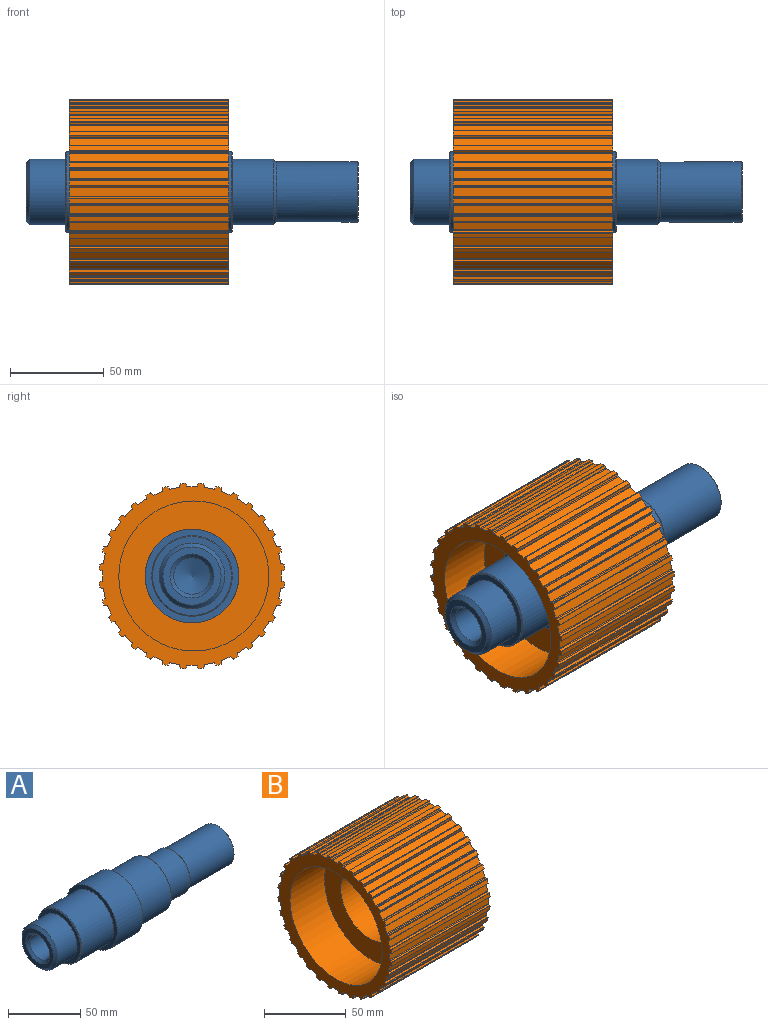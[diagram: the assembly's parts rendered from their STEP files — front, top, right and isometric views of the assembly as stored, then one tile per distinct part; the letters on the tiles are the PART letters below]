
ASSEMBLY  parts=2 mates=1
PART A: 20 faces, bbox 177x50x50 mm
  f0: cylinder r=17.5mm len=35mm, axis (-1,0,0), area 2089.2mm2, adj f14,f15
  f1: plane 31x31mm, normal (-1,0,0), area 321mm2, adj f15,f16
  f2: cylinder r=9.75mm len=92mm, axis (-1,0,0), area 5636mm2, adj f3,f16
  f3: cone r=9.75mm half-angle=70.3deg, axis (-1,0,0), area 317.3mm2, adj f2
  f4: plane 31x31mm, normal (1,0,0), area 754.8mm2, adj f17
  f5: cylinder r=16mm len=43mm, axis (-1,0,0), area 4322.8mm2, adj f6,f17
  f6: torus R=17.5mm, axis (-1,0,0), area 244.9mm2, adj f5,f7
  f7: cylinder r=17.5mm len=35mm, axis (-1,0,0), area 2419mm2, adj f6,f8
  f8: plane 42x42mm, normal (1,0,0), area 423.3mm2, adj f7,f18
  f9: cylinder r=21.5mm len=43mm, axis (-1,0,0), area 4255.3mm2, adj f10,f18
  f10: plane 50x50mm, normal (1,0,0), area 511.3mm2, adj f9,f11
  f11: cylinder r=25mm len=50mm, axis (-1,0,0), area 3927mm2, adj f10,f12
  f12: plane 50x50mm, normal (-1,0,0), area 511.3mm2, adj f11,f13
  f13: cylinder r=21.5mm len=43mm, axis (-1,0,0), area 4255.3mm2, adj f12,f19
  f14: plane 42x42mm, normal (-1,0,0), area 423.3mm2, adj f0,f19
  f15: cone r=15.5mm half-angle=45deg, axis (1,0,0), area 293.2mm2, adj f0,f1
  f16: cone r=9.75mm half-angle=45deg, axis (-1,0,0), area 191mm2, adj f1,f2
  f17: cone r=16mm half-angle=45deg, axis (-1,0,0), area 70mm2, adj f4,f5
  f18: cone r=21.5mm half-angle=45deg, axis (-1,0,0), area 94.4mm2, adj f8,f9
  f19: cone r=21mm half-angle=45deg, axis (1,0,0), area 94.4mm2, adj f13,f14
PART B: 263 faces, bbox 85x98.8x98.8 mm
  f0: cylinder r=0.5mm len=85mm, axis (-1,0,0), area 48.2mm2, adj f219,f220,f224,f257
  f1: cylinder r=0.5mm len=85mm, axis (-1,0,0), area 48.2mm2, adj f215,f216,f224,f257
  f2: cylinder r=0.5mm len=85mm, axis (-1,0,0), area 48.2mm2, adj f211,f212,f224,f257
  f3: cylinder r=0.5mm len=85mm, axis (-1,0,0), area 48.2mm2, adj f207,f208,f224,f257
  f4: cylinder r=0.5mm len=85mm, axis (-1,0,0), area 48.2mm2, adj f53,f203,f224,f257
  f5: cylinder r=0.5mm len=85mm, axis (-1,0,0), area 48.2mm2, adj f199,f202,f224,f257
  f6: cylinder r=0.5mm len=85mm, axis (-1,0,0), area 48.2mm2, adj f195,f198,f224,f257
  f7: cylinder r=0.5mm len=85mm, axis (-1,0,0), area 48.2mm2, adj f191,f194,f224,f257
  f8: cylinder r=0.5mm len=85mm, axis (-1,0,0), area 48.2mm2, adj f163,f164,f224,f257
  f9: cylinder r=0.5mm len=85mm, axis (-1,0,0), area 48.2mm2, adj f159,f160,f224,f257
  f10: cylinder r=0.5mm len=85mm, axis (-1,0,0), area 48.2mm2, adj f155,f156,f224,f257
  f11: cylinder r=0.5mm len=85mm, axis (-1,0,0), area 48.2mm2, adj f151,f152,f224,f257
  f12: cylinder r=0.5mm len=85mm, axis (-1,0,0), area 48.2mm2, adj f147,f148,f224,f257
  f13: cylinder r=0.5mm len=85mm, axis (-1,0,0), area 48.2mm2, adj f137,f140,f224,f257
  f14: cylinder r=0.5mm len=85mm, axis (-1,0,0), area 48.2mm2, adj f133,f136,f224,f257
  f15: cylinder r=0.5mm len=85mm, axis (-1,0,0), area 48.2mm2, adj f129,f132,f224,f257
  f16: cylinder r=0.5mm len=85mm, axis (-1,0,0), area 48.2mm2, adj f125,f128,f224,f257
  f17: cylinder r=0.5mm len=85mm, axis (-1,0,0), area 48.2mm2, adj f121,f124,f224,f257
  f18: cylinder r=0.5mm len=85mm, axis (-1,0,0), area 48.2mm2, adj f94,f223,f224,f257
  f19: cylinder r=1.2mm len=85mm, axis (-1,0,0), area 27.1mm2, adj f208,f224,f256,f257
  f20: cylinder r=1.2mm len=85mm, axis (-1,0,0), area 27.1mm2, adj f202,f224,f229,f257
  f21: cylinder r=1.2mm len=85mm, axis (-1,0,0), area 27.1mm2, adj f198,f224,f230,f257
  f22: cylinder r=1.2mm len=85mm, axis (-1,0,0), area 27.1mm2, adj f194,f224,f231,f257
  f23: cylinder r=1.2mm len=85mm, axis (-1,0,0), area 27.1mm2, adj f164,f224,f236,f257
  f24: cylinder r=1.2mm len=85mm, axis (-1,0,0), area 27.1mm2, adj f160,f224,f237,f257
  f25: cylinder r=1.2mm len=85mm, axis (-1,0,0), area 27.1mm2, adj f156,f224,f238,f257
  f26: cylinder r=1.2mm len=85mm, axis (-1,0,0), area 27.1mm2, adj f152,f224,f239,f257
  f27: cylinder r=1.2mm len=85mm, axis (-1,0,0), area 27.1mm2, adj f148,f224,f240,f257
  f28: cylinder r=1.2mm len=85mm, axis (-1,0,0), area 27.1mm2, adj f145,f224,f242,f257
  f29: cylinder r=1.2mm len=85mm, axis (-1,0,0), area 27.1mm2, adj f144,f224,f241,f257
  f30: cylinder r=1.2mm len=85mm, axis (-1,0,0), area 27.1mm2, adj f140,f224,f243,f257
  f31: cylinder r=1.2mm len=85mm, axis (-1,0,0), area 27.1mm2, adj f136,f224,f244,f257
  f32: cylinder r=1.2mm len=85mm, axis (-1,0,0), area 27.1mm2, adj f132,f224,f245,f257
  f33: cylinder r=1.2mm len=85mm, axis (-1,0,0), area 27.1mm2, adj f128,f224,f246,f257
  f34: cylinder r=1.2mm len=85mm, axis (-1,0,0), area 27.1mm2, adj f124,f224,f247,f257
  f35: cylinder r=1.2mm len=85mm, axis (-1,0,0), area 27.1mm2, adj f94,f224,f252,f257
  f36: cylinder r=1.2mm len=85mm, axis (-1,0,0), area 27.1mm2, adj f220,f224,f253,f257
  f37: cylinder r=1.2mm len=85mm, axis (-1,0,0), area 27.1mm2, adj f216,f224,f254,f257
  f38: cylinder r=1.2mm len=85mm, axis (-1,0,0), area 27.1mm2, adj f212,f224,f255,f257
  f39: cylinder r=1.2mm len=85mm, axis (-1,0,0), area 27.1mm2, adj f53,f224,f228,f257
  f40: cylinder r=0.5mm len=85mm, axis (-1,0,0), area 48.2mm2, adj f52,f205,f224,f257
  f41: cylinder r=1.2mm len=85mm, axis (-1,0,0), area 27.1mm2, adj f205,f224,f227,f257
  f42: cylinder r=1.2mm len=85mm, axis (-1,0,0), area 27.1mm2, adj f44,f224,f226,f257
  f43: cylinder r=1.2mm len=85mm, axis (-1,0,0), area 27.1mm2, adj f45,f224,f225,f257
  f44: plane 85x1.17mm, normal (0,0.91,0.42), area 110mm2, adj f42,f48,f224,f257
  f45: plane 85x1.17mm, normal (0,-0.91,0.42), area 110mm2, adj f43,f46,f224,f257
  f46: cylinder r=0.5mm len=85mm, axis (-1,0,0), area 48.2mm2, adj f45,f47,f224,f257
  f47: plane 85x4.54mm, normal (0,0,1), area 386.2mm2, adj f46,f48,f224,f257
  f48: cylinder r=0.5mm len=85mm, axis (-1,0,0), area 48.2mm2, adj f44,f47,f224,f257
  f49: cylinder r=1.2mm len=85mm, axis (-1,0,0), area 27.1mm2, adj f50,f224,f226,f257
  f50: plane 85x1.26mm, normal (0,-0.97,0.24), area 110mm2, adj f49,f51,f224,f257
  f51: cylinder r=0.5mm len=85mm, axis (-1,0,0), area 48.2mm2, adj f50,f52,f224,f257
  f52: plane 85x4.46mm, normal (0,-0.2,0.98), area 386.2mm2, adj f40,f51,f224,f257
  f53: plane 85x0.95mm, normal (0,0.68,0.74), area 110mm2, adj f4,f39,f224,f257
  f54: plane 85x1.29mm, normal (0,-1,0.04), area 110mm2, adj f55,f204,f224,f257
  f55: cylinder r=1.2mm len=85mm, axis (-1,0,0), area 27.1mm2, adj f54,f224,f227,f257
  f56: cylinder r=1.2mm len=85mm, axis (-1,0,0), area 27.1mm2, adj f213,f224,f256,f257
  f57: cylinder r=1.2mm len=85mm, axis (-1,0,0), area 27.1mm2, adj f217,f224,f255,f257
  f58: cylinder r=1.2mm len=85mm, axis (-1,0,0), area 27.1mm2, adj f221,f224,f254,f257
  f59: cylinder r=1.2mm len=85mm, axis (-1,0,0), area 27.1mm2, adj f95,f224,f253,f257
  f60: cylinder r=1.2mm len=85mm, axis (-1,0,0), area 27.1mm2, adj f99,f224,f251,f257
  f61: cylinder r=1.2mm len=85mm, axis (-1,0,0), area 27.1mm2, adj f100,f224,f252,f257
  f62: cylinder r=1.2mm len=85mm, axis (-1,0,0), area 27.1mm2, adj f104,f224,f250,f257
  f63: cylinder r=1.2mm len=85mm, axis (-1,0,0), area 27.1mm2, adj f105,f224,f251,f257
  f64: cylinder r=1.2mm len=85mm, axis (-1,0,0), area 27.1mm2, adj f109,f224,f249,f257
  f65: cylinder r=1.2mm len=85mm, axis (-1,0,0), area 27.1mm2, adj f110,f224,f250,f257
  f66: cylinder r=1.2mm len=85mm, axis (-1,0,0), area 27.1mm2, adj f114,f224,f248,f257
  f67: cylinder r=1.2mm len=85mm, axis (-1,0,0), area 27.1mm2, adj f115,f224,f249,f257
  f68: cylinder r=1.2mm len=85mm, axis (-1,0,0), area 27.1mm2, adj f119,f224,f247,f257
  f69: cylinder r=1.2mm len=85mm, axis (-1,0,0), area 27.1mm2, adj f120,f224,f248,f257
  f70: cylinder r=1.2mm len=85mm, axis (-1,0,0), area 27.1mm2, adj f123,f224,f246,f257
  f71: cylinder r=1.2mm len=85mm, axis (-1,0,0), area 27.1mm2, adj f127,f224,f245,f257
  f72: cylinder r=1.2mm len=85mm, axis (-1,0,0), area 27.1mm2, adj f131,f224,f244,f257
  f73: cylinder r=1.2mm len=85mm, axis (-1,0,0), area 27.1mm2, adj f135,f224,f243,f257
  f74: cylinder r=1.2mm len=85mm, axis (-1,0,0), area 27.1mm2, adj f139,f224,f242,f257
  f75: cylinder r=1.2mm len=85mm, axis (-1,0,0), area 27.1mm2, adj f149,f224,f241,f257
  f76: cylinder r=1.2mm len=85mm, axis (-1,0,0), area 27.1mm2, adj f153,f224,f240,f257
  f77: cylinder r=1.2mm len=85mm, axis (-1,0,0), area 27.1mm2, adj f157,f224,f239,f257
  f78: cylinder r=1.2mm len=85mm, axis (-1,0,0), area 27.1mm2, adj f161,f224,f238,f257
  f79: cylinder r=1.2mm len=85mm, axis (-1,0,0), area 27.1mm2, adj f165,f224,f237,f257
  f80: cylinder r=1.2mm len=85mm, axis (-1,0,0), area 27.1mm2, adj f169,f224,f235,f257
  f81: cylinder r=1.2mm len=85mm, axis (-1,0,0), area 27.1mm2, adj f170,f224,f236,f257
  f82: cylinder r=1.2mm len=85mm, axis (-1,0,0), area 27.1mm2, adj f174,f224,f234,f257
  f83: cylinder r=1.2mm len=85mm, axis (-1,0,0), area 27.1mm2, adj f175,f224,f235,f257
  f84: cylinder r=1.2mm len=85mm, axis (-1,0,0), area 27.1mm2, adj f179,f224,f233,f257
  f85: cylinder r=1.2mm len=85mm, axis (-1,0,0), area 27.1mm2, adj f180,f224,f234,f257
  f86: cylinder r=1.2mm len=85mm, axis (-1,0,0), area 27.1mm2, adj f184,f224,f232,f257
  f87: cylinder r=1.2mm len=85mm, axis (-1,0,0), area 27.1mm2, adj f185,f224,f233,f257
  f88: cylinder r=1.2mm len=85mm, axis (-1,0,0), area 27.1mm2, adj f189,f224,f231,f257
  f89: cylinder r=1.2mm len=85mm, axis (-1,0,0), area 27.1mm2, adj f190,f224,f232,f257
  f90: cylinder r=1.2mm len=85mm, axis (-1,0,0), area 27.1mm2, adj f193,f224,f230,f257
  f91: cylinder r=1.2mm len=85mm, axis (-1,0,0), area 27.1mm2, adj f197,f224,f229,f257
  f92: cylinder r=1.2mm len=85mm, axis (-1,0,0), area 27.1mm2, adj f201,f224,f228,f257
  f93: cylinder r=1.2mm len=85mm, axis (-1,0,0), area 27.1mm2, adj f209,f224,f225,f257
  f94: plane 85x1.28mm, normal (0,-0.15,0.99), area 110mm2, adj f18,f35,f224,f257
  f95: plane 85x1.11mm, normal (0,0.85,-0.52), area 110mm2, adj f59,f222,f224,f257
  f96: cylinder r=0.5mm len=85mm, axis (-1,0,0), area 48.2mm2, adj f97,f100,f224,f257
  f97: plane 85x4.2mm, normal (0,0.92,0.38), area 386.2mm2, adj f96,f98,f224,f257
  f98: cylinder r=0.5mm len=85mm, axis (-1,0,0), area 48.2mm2, adj f97,f99,f224,f257
  f99: plane 85x1.29mm, normal (0,0.04,1), area 110mm2, adj f60,f98,f224,f257
  f100: plane 85x0.95mm, normal (0,0.74,-0.68), area 110mm2, adj f61,f96,f224,f257
  f101: cylinder r=0.5mm len=85mm, axis (-1,0,0), area 48.2mm2, adj f102,f105,f224,f257
  f102: plane 85x4.46mm, normal (0,0.98,0.2), area 386.2mm2, adj f101,f103,f224,f257
  f103: cylinder r=0.5mm len=85mm, axis (-1,0,0), area 48.2mm2, adj f102,f104,f224,f257
  f104: plane 85x1.26mm, normal (0,0.24,0.97), area 110mm2, adj f62,f103,f224,f257
  f105: plane 85x1.04mm, normal (0,0.59,-0.81), area 110mm2, adj f63,f101,f224,f257
  f106: cylinder r=0.5mm len=85mm, axis (-1,0,0), area 48.2mm2, adj f107,f110,f224,f257
  f107: plane 85x4.54mm, normal (0,1,0), area 386.2mm2, adj f106,f108,f224,f257
  f108: cylinder r=0.5mm len=85mm, axis (-1,0,0), area 48.2mm2, adj f107,f109,f224,f257
  f109: plane 85x1.17mm, normal (0,0.42,0.91), area 110mm2, adj f64,f108,f224,f257
  f110: plane 85x1.17mm, normal (0,0.42,-0.91), area 110mm2, adj f65,f106,f224,f257
  f111: cylinder r=0.5mm len=85mm, axis (-1,0,0), area 48.2mm2, adj f112,f115,f224,f257
  f112: plane 85x4.46mm, normal (0,0.98,-0.2), area 386.2mm2, adj f111,f113,f224,f257
  f113: cylinder r=0.5mm len=85mm, axis (-1,0,0), area 48.2mm2, adj f112,f114,f224,f257
  f114: plane 85x1.04mm, normal (0,0.59,0.81), area 110mm2, adj f66,f113,f224,f257
  f115: plane 85x1.26mm, normal (0,0.24,-0.97), area 110mm2, adj f67,f111,f224,f257
  f116: cylinder r=0.5mm len=85mm, axis (-1,0,0), area 48.2mm2, adj f117,f120,f224,f257
  f117: plane 85x4.2mm, normal (0,0.92,-0.38), area 386.2mm2, adj f116,f118,f224,f257
  f118: cylinder r=0.5mm len=85mm, axis (-1,0,0), area 48.2mm2, adj f117,f119,f224,f257
  f119: plane 85x0.95mm, normal (0,0.74,0.68), area 110mm2, adj f68,f118,f224,f257
  f120: plane 85x1.29mm, normal (0,0.04,-1), area 110mm2, adj f69,f116,f224,f257
  f121: plane 85x3.78mm, normal (0,0.83,-0.56), area 386.2mm2, adj f17,f122,f224,f257
  f122: cylinder r=0.5mm len=85mm, axis (-1,0,0), area 48.2mm2, adj f121,f123,f224,f257
  f123: plane 85x1.11mm, normal (0,0.85,0.52), area 110mm2, adj f70,f122,f224,f257
  f124: plane 85x1.28mm, normal (0,-0.15,-0.99), area 110mm2, adj f17,f34,f224,f257
  f125: plane 85x3.21mm, normal (0,0.71,-0.71), area 386.2mm2, adj f16,f126,f224,f257
  f126: cylinder r=0.5mm len=85mm, axis (-1,0,0), area 48.2mm2, adj f125,f127,f224,f257
  f127: plane 85x1.22mm, normal (0,0.94,0.34), area 110mm2, adj f71,f126,f224,f257
  f128: plane 85x1.22mm, normal (0,-0.34,-0.94), area 110mm2, adj f16,f33,f224,f257
  f129: plane 85x3.78mm, normal (0,0.56,-0.83), area 386.2mm2, adj f15,f130,f224,f257
  f130: cylinder r=0.5mm len=85mm, axis (-1,0,0), area 48.2mm2, adj f129,f131,f224,f257
  f131: plane 85x1.28mm, normal (0,0.99,0.15), area 110mm2, adj f72,f130,f224,f257
  f132: plane 85x1.11mm, normal (0,-0.52,-0.85), area 110mm2, adj f15,f32,f224,f257
  f133: plane 85x4.2mm, normal (0,0.38,-0.92), area 386.2mm2, adj f14,f134,f224,f257
  f134: cylinder r=0.5mm len=85mm, axis (-1,0,0), area 48.2mm2, adj f133,f135,f224,f257
  f135: plane 85x1.29mm, normal (0,1,-0.04), area 110mm2, adj f73,f134,f224,f257
  f136: plane 85x0.95mm, normal (0,-0.68,-0.74), area 110mm2, adj f14,f31,f224,f257
  f137: plane 85x4.46mm, normal (0,0.2,-0.98), area 386.2mm2, adj f13,f138,f224,f257
  f138: cylinder r=0.5mm len=85mm, axis (-1,0,0), area 48.2mm2, adj f137,f139,f224,f257
  f139: plane 85x1.26mm, normal (0,0.97,-0.24), area 110mm2, adj f74,f138,f224,f257
  f140: plane 85x1.04mm, normal (0,-0.81,-0.59), area 110mm2, adj f13,f30,f224,f257
  f141: cylinder r=0.5mm len=85mm, axis (-1,0,0), area 48.2mm2, adj f142,f145,f224,f257
  f142: plane 85x4.54mm, normal (0,0,-1), area 386.2mm2, adj f141,f143,f224,f257
  f143: cylinder r=0.5mm len=85mm, axis (-1,0,0), area 48.2mm2, adj f142,f144,f224,f257
  f144: plane 85x1.17mm, normal (0,0.91,-0.42), area 110mm2, adj f29,f143,f224,f257
  f145: plane 85x1.17mm, normal (0,-0.91,-0.42), area 110mm2, adj f28,f141,f224,f257
  f146: cylinder r=0.5mm len=85mm, axis (-1,0,0), area 48.2mm2, adj f147,f149,f224,f257
  f147: plane 85x4.46mm, normal (0,-0.2,-0.98), area 386.2mm2, adj f12,f146,f224,f257
  f148: plane 85x1.04mm, normal (0,0.81,-0.59), area 110mm2, adj f12,f27,f224,f257
  f149: plane 85x1.26mm, normal (0,-0.97,-0.24), area 110mm2, adj f75,f146,f224,f257
  f150: cylinder r=0.5mm len=85mm, axis (-1,0,0), area 48.2mm2, adj f151,f153,f224,f257
  f151: plane 85x4.2mm, normal (0,-0.38,-0.92), area 386.2mm2, adj f11,f150,f224,f257
  f152: plane 85x0.95mm, normal (0,0.68,-0.74), area 110mm2, adj f11,f26,f224,f257
  f153: plane 85x1.29mm, normal (0,-1,-0.04), area 110mm2, adj f76,f150,f224,f257
  f154: cylinder r=0.5mm len=85mm, axis (-1,0,0), area 48.2mm2, adj f155,f157,f224,f257
  f155: plane 85x3.78mm, normal (0,-0.56,-0.83), area 386.2mm2, adj f10,f154,f224,f257
  f156: plane 85x1.11mm, normal (0,0.52,-0.85), area 110mm2, adj f10,f25,f224,f257
  f157: plane 85x1.28mm, normal (0,-0.99,0.15), area 110mm2, adj f77,f154,f224,f257
  f158: cylinder r=0.5mm len=85mm, axis (-1,0,0), area 48.2mm2, adj f159,f161,f224,f257
  f159: plane 85x3.21mm, normal (0,-0.71,-0.71), area 386.2mm2, adj f9,f158,f224,f257
  f160: plane 85x1.22mm, normal (0,0.34,-0.94), area 110mm2, adj f9,f24,f224,f257
  f161: plane 85x1.22mm, normal (0,-0.94,0.34), area 110mm2, adj f78,f158,f224,f257
  f162: cylinder r=0.5mm len=85mm, axis (-1,0,0), area 48.2mm2, adj f163,f165,f224,f257
  f163: plane 85x3.78mm, normal (0,-0.83,-0.56), area 386.2mm2, adj f8,f162,f224,f257
  f164: plane 85x1.28mm, normal (0,0.15,-0.99), area 110mm2, adj f8,f23,f224,f257
  f165: plane 85x1.11mm, normal (0,-0.85,0.52), area 110mm2, adj f79,f162,f224,f257
  f166: cylinder r=0.5mm len=85mm, axis (-1,0,0), area 48.2mm2, adj f167,f170,f224,f257
  f167: plane 85x4.2mm, normal (0,-0.92,-0.38), area 386.2mm2, adj f166,f168,f224,f257
  f168: cylinder r=0.5mm len=85mm, axis (-1,0,0), area 48.2mm2, adj f167,f169,f224,f257
  f169: plane 85x1.29mm, normal (0,-0.04,-1), area 110mm2, adj f80,f168,f224,f257
  f170: plane 85x0.95mm, normal (0,-0.74,0.68), area 110mm2, adj f81,f166,f224,f257
  f171: cylinder r=0.5mm len=85mm, axis (-1,0,0), area 48.2mm2, adj f172,f175,f224,f257
  f172: plane 85x4.46mm, normal (0,-0.98,-0.2), area 386.2mm2, adj f171,f173,f224,f257
  f173: cylinder r=0.5mm len=85mm, axis (-1,0,0), area 48.2mm2, adj f172,f174,f224,f257
  f174: plane 85x1.26mm, normal (0,-0.24,-0.97), area 110mm2, adj f82,f173,f224,f257
  f175: plane 85x1.04mm, normal (0,-0.59,0.81), area 110mm2, adj f83,f171,f224,f257
  f176: cylinder r=0.5mm len=85mm, axis (-1,0,0), area 48.2mm2, adj f177,f180,f224,f257
  f177: plane 85x4.54mm, normal (0,-1,0), area 386.2mm2, adj f176,f178,f224,f257
  f178: cylinder r=0.5mm len=85mm, axis (-1,0,0), area 48.2mm2, adj f177,f179,f224,f257
  f179: plane 85x1.17mm, normal (0,-0.42,-0.91), area 110mm2, adj f84,f178,f224,f257
  f180: plane 85x1.17mm, normal (0,-0.42,0.91), area 110mm2, adj f85,f176,f224,f257
  f181: cylinder r=0.5mm len=85mm, axis (-1,0,0), area 48.2mm2, adj f182,f185,f224,f257
  f182: plane 85x4.46mm, normal (0,-0.98,0.2), area 386.2mm2, adj f181,f183,f224,f257
  f183: cylinder r=0.5mm len=85mm, axis (-1,0,0), area 48.2mm2, adj f182,f184,f224,f257
  f184: plane 85x1.04mm, normal (0,-0.59,-0.81), area 110mm2, adj f86,f183,f224,f257
  f185: plane 85x1.26mm, normal (0,-0.24,0.97), area 110mm2, adj f87,f181,f224,f257
  f186: cylinder r=0.5mm len=85mm, axis (-1,0,0), area 48.2mm2, adj f187,f190,f224,f257
  f187: plane 85x4.2mm, normal (0,-0.92,0.38), area 386.2mm2, adj f186,f188,f224,f257
  f188: cylinder r=0.5mm len=85mm, axis (-1,0,0), area 48.2mm2, adj f187,f189,f224,f257
  f189: plane 85x0.95mm, normal (0,-0.74,-0.68), area 110mm2, adj f88,f188,f224,f257
  f190: plane 85x1.29mm, normal (0,-0.04,1), area 110mm2, adj f89,f186,f224,f257
  f191: plane 85x3.78mm, normal (0,-0.83,0.56), area 386.2mm2, adj f7,f192,f224,f257
  f192: cylinder r=0.5mm len=85mm, axis (-1,0,0), area 48.2mm2, adj f191,f193,f224,f257
  f193: plane 85x1.11mm, normal (0,-0.85,-0.52), area 110mm2, adj f90,f192,f224,f257
  f194: plane 85x1.28mm, normal (0,0.15,0.99), area 110mm2, adj f7,f22,f224,f257
  f195: plane 85x3.21mm, normal (0,-0.71,0.71), area 386.2mm2, adj f6,f196,f224,f257
  f196: cylinder r=0.5mm len=85mm, axis (-1,0,0), area 48.2mm2, adj f195,f197,f224,f257
  f197: plane 85x1.22mm, normal (0,-0.94,-0.34), area 110mm2, adj f91,f196,f224,f257
  f198: plane 85x1.22mm, normal (0,0.34,0.94), area 110mm2, adj f6,f21,f224,f257
  f199: plane 85x3.78mm, normal (0,-0.56,0.83), area 386.2mm2, adj f5,f200,f224,f257
  f200: cylinder r=0.5mm len=85mm, axis (-1,0,0), area 48.2mm2, adj f199,f201,f224,f257
  f201: plane 85x1.28mm, normal (0,-0.99,-0.15), area 110mm2, adj f92,f200,f224,f257
  f202: plane 85x1.11mm, normal (0,0.52,0.85), area 110mm2, adj f5,f20,f224,f257
  f203: plane 85x4.2mm, normal (0,-0.38,0.92), area 386.2mm2, adj f4,f204,f224,f257
  f204: cylinder r=0.5mm len=85mm, axis (-1,0,0), area 48.2mm2, adj f54,f203,f224,f257
  f205: plane 85x1.04mm, normal (0,0.81,0.59), area 110mm2, adj f40,f41,f224,f257
  f206: cylinder r=0.5mm len=85mm, axis (-1,0,0), area 48.2mm2, adj f207,f209,f224,f257
  f207: plane 85x4.46mm, normal (0,0.2,0.98), area 386.2mm2, adj f3,f206,f224,f257
  f208: plane 85x1.04mm, normal (0,-0.81,0.59), area 110mm2, adj f3,f19,f224,f257
  f209: plane 85x1.26mm, normal (0,0.97,0.24), area 110mm2, adj f93,f206,f224,f257
  f210: cylinder r=0.5mm len=85mm, axis (-1,0,0), area 48.2mm2, adj f211,f213,f224,f257
  f211: plane 85x4.2mm, normal (0,0.38,0.92), area 386.2mm2, adj f2,f210,f224,f257
  f212: plane 85x0.95mm, normal (0,-0.68,0.74), area 110mm2, adj f2,f38,f224,f257
  f213: plane 85x1.29mm, normal (0,1,0.04), area 110mm2, adj f56,f210,f224,f257
  f214: cylinder r=0.5mm len=85mm, axis (-1,0,0), area 48.2mm2, adj f215,f217,f224,f257
  f215: plane 85x3.78mm, normal (0,0.56,0.83), area 386.2mm2, adj f1,f214,f224,f257
  f216: plane 85x1.11mm, normal (0,-0.52,0.85), area 110mm2, adj f1,f37,f224,f257
  f217: plane 85x1.28mm, normal (0,0.99,-0.15), area 110mm2, adj f57,f214,f224,f257
  f218: cylinder r=0.5mm len=85mm, axis (-1,0,0), area 48.2mm2, adj f219,f221,f224,f257
  f219: plane 85x3.21mm, normal (0,0.71,0.71), area 386.2mm2, adj f0,f218,f224,f257
  f220: plane 85x1.22mm, normal (0,-0.34,0.94), area 110mm2, adj f0,f36,f224,f257
  f221: plane 85x1.22mm, normal (0,0.94,-0.34), area 110mm2, adj f58,f218,f224,f257
  f222: cylinder r=0.5mm len=85mm, axis (-1,0,0), area 48.2mm2, adj f95,f223,f224,f257
  f223: plane 85x3.78mm, normal (0,0.83,0.56), area 386.2mm2, adj f18,f222,f224,f257
  f224: plane 98.76x98.76mm, normal (1,0,0), area 2322.9mm2, adj f0,f1,f2,f3,f4,f5,f6,f7
  f225: cylinder r=49.5mm len=85mm, axis (1,0,0), area 240.2mm2, adj f43,f93,f224,f257
  f226: cylinder r=49.5mm len=85mm, axis (1,0,0), area 240.2mm2, adj f42,f49,f224,f257
  f227: cylinder r=49.5mm len=85mm, axis (1,0,0), area 240.2mm2, adj f41,f55,f224,f257
  f228: cylinder r=49.5mm len=85mm, axis (1,0,0), area 240.2mm2, adj f39,f92,f224,f257
  f229: cylinder r=49.5mm len=85mm, axis (1,0,0), area 240.2mm2, adj f20,f91,f224,f257
  f230: cylinder r=49.5mm len=85mm, axis (1,0,0), area 240.2mm2, adj f21,f90,f224,f257
  f231: cylinder r=49.5mm len=85mm, axis (1,0,0), area 240.2mm2, adj f22,f88,f224,f257
  f232: cylinder r=49.5mm len=85mm, axis (1,0,0), area 240.2mm2, adj f86,f89,f224,f257
  f233: cylinder r=49.5mm len=85mm, axis (1,0,0), area 240.2mm2, adj f84,f87,f224,f257
  f234: cylinder r=49.5mm len=85mm, axis (1,0,0), area 240.2mm2, adj f82,f85,f224,f257
  f235: cylinder r=49.5mm len=85mm, axis (1,0,0), area 240.2mm2, adj f80,f83,f224,f257
  f236: cylinder r=49.5mm len=85mm, axis (1,0,0), area 240.2mm2, adj f23,f81,f224,f257
  f237: cylinder r=49.5mm len=85mm, axis (1,0,0), area 240.2mm2, adj f24,f79,f224,f257
  f238: cylinder r=49.5mm len=85mm, axis (1,0,0), area 240.2mm2, adj f25,f78,f224,f257
  f239: cylinder r=49.5mm len=85mm, axis (1,0,0), area 240.2mm2, adj f26,f77,f224,f257
  f240: cylinder r=49.5mm len=85mm, axis (1,0,0), area 240.2mm2, adj f27,f76,f224,f257
  f241: cylinder r=49.5mm len=85mm, axis (1,0,0), area 240.2mm2, adj f29,f75,f224,f257
  f242: cylinder r=49.5mm len=85mm, axis (1,0,0), area 240.2mm2, adj f28,f74,f224,f257
  f243: cylinder r=49.5mm len=85mm, axis (1,0,0), area 240.2mm2, adj f30,f73,f224,f257
  f244: cylinder r=49.5mm len=85mm, axis (1,0,0), area 240.2mm2, adj f31,f72,f224,f257
  f245: cylinder r=49.5mm len=85mm, axis (1,0,0), area 240.2mm2, adj f32,f71,f224,f257
  f246: cylinder r=49.5mm len=85mm, axis (1,0,0), area 240.2mm2, adj f33,f70,f224,f257
  f247: cylinder r=49.5mm len=85mm, axis (1,0,0), area 240.2mm2, adj f34,f68,f224,f257
  f248: cylinder r=49.5mm len=85mm, axis (1,0,0), area 240.2mm2, adj f66,f69,f224,f257
  f249: cylinder r=49.5mm len=85mm, axis (1,0,0), area 240.2mm2, adj f64,f67,f224,f257
  f250: cylinder r=49.5mm len=85mm, axis (1,0,0), area 240.2mm2, adj f62,f65,f224,f257
  f251: cylinder r=49.5mm len=85mm, axis (1,0,0), area 240.2mm2, adj f60,f63,f224,f257
  f252: cylinder r=49.5mm len=85mm, axis (1,0,0), area 240.2mm2, adj f35,f61,f224,f257
  f253: cylinder r=49.5mm len=85mm, axis (1,0,0), area 240.2mm2, adj f36,f59,f224,f257
  f254: cylinder r=49.5mm len=85mm, axis (1,0,0), area 240.2mm2, adj f37,f58,f224,f257
  f255: cylinder r=49.5mm len=85mm, axis (1,0,0), area 240.2mm2, adj f38,f57,f224,f257
  f256: cylinder r=49.5mm len=85mm, axis (1,0,0), area 240.2mm2, adj f19,f56,f224,f257
  f257: plane 98.76x98.76mm, normal (-1,0,0), area 2322.9mm2, adj f0,f1,f2,f3,f4,f5,f6,f7
  f258: cylinder r=40mm len=80mm, axis (-1,0,0), area 7539.8mm2, adj f257,f259
  f259: plane 80x80mm, normal (-1,0,0), area 3063.1mm2, adj f258,f262
  f260: cylinder r=40mm len=80mm, axis (1,0,0), area 7539.8mm2, adj f224,f261
  f261: plane 80x80mm, normal (1,0,0), area 3063.1mm2, adj f260,f262
  f262: cylinder r=25mm len=50mm, axis (1,0,0), area 3927mm2, adj f259,f261
PLACE A t=(32.18,73.08,25.02)mm
PLACE B t=(-59.82,73.08,25.02)mm
MATE fastened A.f19 <-> B.f260  axis (1,0,0) through (110.18,73.08,25.02)mm
